# Revit family: Haworth_Planes_CartMedia_Medium_AP_PRELIMINARY
name_source: partatom
category: Furniture Systems
units: mm (PartAtom-declared; Revit-internal decimal feet)

## family parameters
Always vertical = Yes
Cut with Voids When Loaded = No
OmniClass Number = 23.40.70.14.64.21.14
OmniClass Title = Free-Standing Component
Part Type = Normal
Room Calculation Point = No
Round Connector Dimension = Use Diameter
Shared = No
Work Plane-Based = No

## types (1)
- Cart - Media Medium
    Actual Depth = 483 mm
    Actual Height = 914 mm
    Actual Width = 483 mm
    Assembly Code = E2020200
    Caster Finish = Haworth _ Paint _ Metallic Champagne
    Casters = Yes
    Description = Haworth - Planes - Cart - Media Medium
    Glides = No
    Leg Thickness = 22 mm
    Manufacturer = Haworth
    Model = WOPLCBM
    Revision = 2
    Shelf Offset = 2 mm  [stored 0.00656168 ft]
    Shelf Thickness = 19 mm
    Side Panel Offset = 13 mm
    Size = Verify Final Dim. w/Haworth
    Top Opening Height = 140 mm
    URL = https://www.haworth.com
    URL - Product = https://www.haworth.com
    Warranty = http://www.haworth.com
    with Lock = Yes

note: [stored X ft] marks values corroborated as IEEE doubles in the binary element streams (Revit-internal decimal feet)

## geometry (parser evidence)
native form markers: Sweep x5
no freeform markers — native parametric forms only
